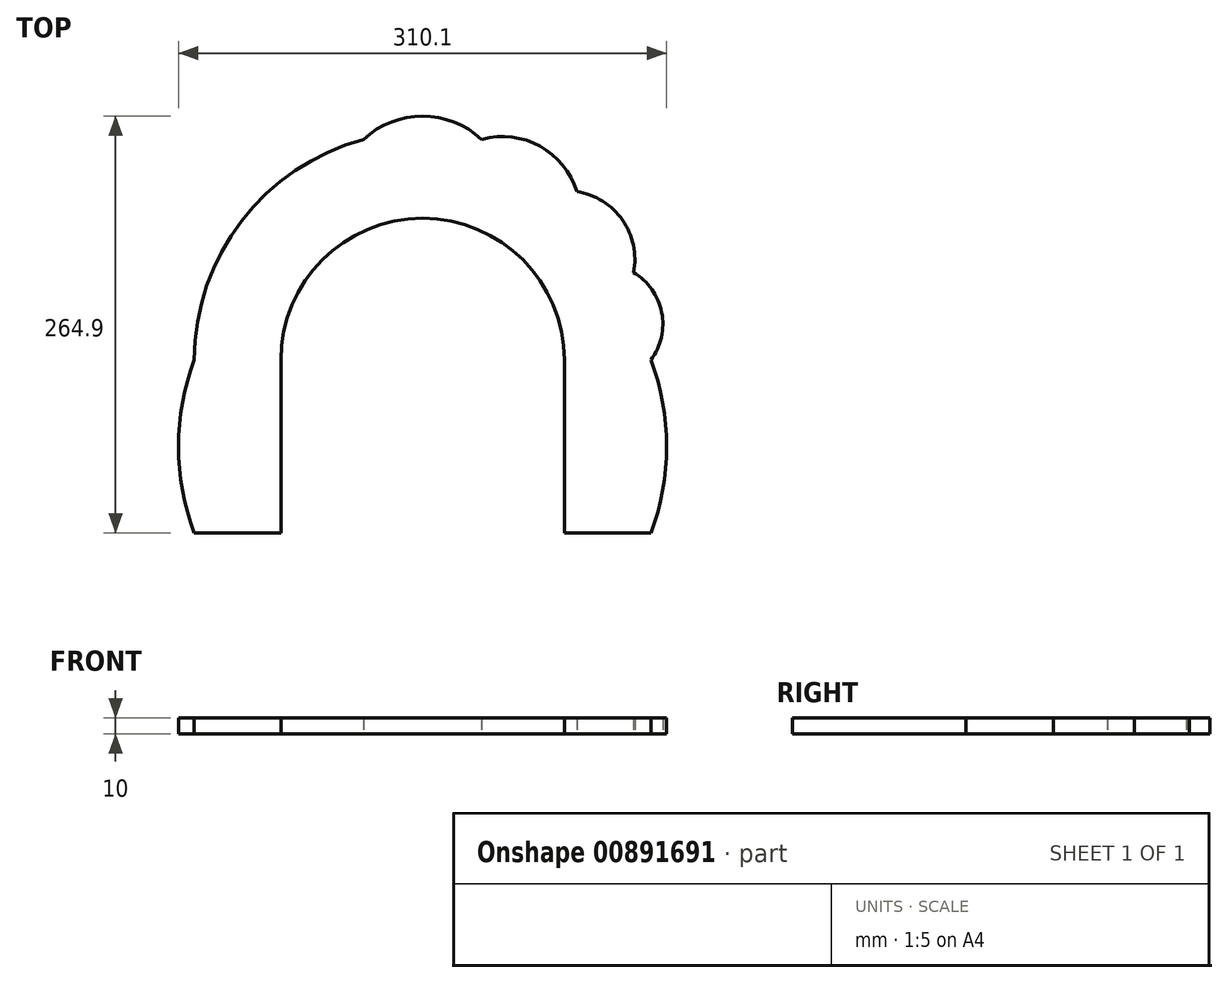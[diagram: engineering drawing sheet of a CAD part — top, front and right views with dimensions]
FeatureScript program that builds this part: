
annotation { "Feature Type Name" : "Feature", "Feature Type Description" : "" }
export const myFeature = defineFeature(function(context is Context, id is Id, definition is map)
    precondition{}
    {
        {
            var Q0;
            Q0=qCreatedBy(makeId("Top.planeOp"),FACE);
            var sketch = newSketch(context, id + "F0", { "sketchPlane" : qUnion([Q0])});
            skFitSpline(sketch, "E0.0.0", {"points": [v(222.24, 427.22) * mm, v(215.5, 429.07) * mm, v(196.44, 434.28) * mm, v(159.63, 464.69) * mm, v(135.76, 484.28) * mm]});
            skArc(sketch, "E0.0.1", {"start": v(135.76, 484.28) * mm, "mid": v(0, 567.46) * mm, "end": v(-135.76, 484.28) * mm});
            skFitSpline(sketch, "E0.0.2", {"points": [v(-135.76, 484.28) * mm, v(-159.63, 464.69) * mm, v(-196.44, 434.28) * mm, v(-215.5, 429.07) * mm, v(-222.24, 427.22) * mm]});
            skFitSpline(sketch, "E0.0.3", {"points": [v(-222.24, 427.22) * mm, v(-225.16, 426.83) * mm, v(-230.26, 426.14) * mm, v(-241.5, 428) * mm, v(-248.93, 433.28) * mm, v(-251.17, 448.34) * mm, v(-240.81, 458.85) * mm, v(-228.97, 457.5) * mm, v(-213.8, 449.01) * mm, v(-232.53, 431.49) * mm, v(-211.41, 442.33) * mm, v(-207.14, 460.38) * mm, v(-224.77, 474.32) * mm, v(-243.2, 474.95) * mm, v(-261.09, 471.32) * mm, v(-274.5, 457.58) * mm, v(-276.7, 439.28) * mm, v(-273.51, 422.75) * mm, v(-283.7, 412.03) * mm, v(-291.16, 413.34) * mm, v(-288.14, 420.98) * mm, v(-292.96, 429.6) * mm, v(-309.4, 438.45) * mm, v(-332.6, 439.06) * mm, v(-351.6, 426.46) * mm, v(-359.68, 415.35) * mm, v(-362.45, 400.5) * mm, v(-361.53, 389.94) * mm, v(-359.47, 382.27) * mm, v(-356.53, 382.37) * mm, v(-352.55, 399.36) * mm, v(-340.04, 407) * mm, v(-328.58, 408.28) * mm, v(-311.3, 404.6) * mm, v(-307.8, 389.6) * mm, v(-312.22, 380.89) * mm, v(-314.05, 379.09) * mm]});
            skArc(sketch, "E0.0.4", {"start": v(-309.42, 390.28) * mm, "mid": v(-312.68, 382.2) * mm, "end": v(-319.87, 377.3) * mm});
            skFitSpline(sketch, "E0.0.5", {"points": [v(-314.05, 379.09) * mm, v(-349.26, 368.46) * mm, v(-392.1, 351.55) * mm, v(-410.06, 337.43) * mm]});
            skEllipticalArc(sketch, "E0.0.6", {});
            skArc(sketch, "E0.0.7", {"start": v(-404.46, 196.44) * mm, "mid": v(-395.87, 191.21) * mm, "end": v(-386.4, 187.8) * mm});
            skFitSpline(sketch, "E0.0.8", {"points": [v(-394.78, 189.9) * mm, v(-344.92, 177.5) * mm, v(-241.75, 151.88) * mm, v(-181.26, 51.75) * mm, v(-150, 0) * mm]});
            skLineSegment(sketch, "E0.0.9", {"start": v(-150, 0) * mm, "end": v(-90, 0) * mm});
            skLineSegment(sketch, "E0.0.10", {"start": v(-90, 0) * mm, "end": v(-90, 110) * mm});
            skArc(sketch, "E0.0.11", {"start": v(-90, 110) * mm, "mid": v(0, 200) * mm, "end": v(90, 110) * mm});
            skLineSegment(sketch, "E0.0.12", {"start": v(90, 110) * mm, "end": v(90, 0) * mm});
            skLineSegment(sketch, "E0.0.13", {"start": v(90, 0) * mm, "end": v(150, 0) * mm});
            skFitSpline(sketch, "E0.0.14", {"points": [v(150, 0) * mm, v(181.26, 51.75) * mm, v(241.75, 151.88) * mm, v(344.92, 177.5) * mm, v(394.78, 189.9) * mm]});
            skArc(sketch, "E0.0.15", {"start": v(386.4, 187.8) * mm, "mid": v(395.87, 191.21) * mm, "end": v(404.46, 196.44) * mm});
            skEllipticalArc(sketch, "E0.0.16", {});
            skFitSpline(sketch, "E0.0.17", {"points": [v(410.06, 337.43) * mm, v(392.1, 351.55) * mm, v(349.26, 368.46) * mm, v(314.05, 379.09) * mm]});
            skArc(sketch, "E0.0.18", {"start": v(319.87, 377.3) * mm, "mid": v(312.68, 382.2) * mm, "end": v(309.42, 390.28) * mm});
            skFitSpline(sketch, "E0.0.19", {"points": [v(314.05, 379.09) * mm, v(312.22, 380.89) * mm, v(307.8, 389.6) * mm, v(311.3, 404.6) * mm, v(328.58, 408.28) * mm, v(340.04, 407) * mm, v(352.55, 399.36) * mm, v(356.53, 382.37) * mm, v(359.47, 382.27) * mm, v(361.53, 389.94) * mm, v(362.45, 400.5) * mm, v(359.68, 415.35) * mm, v(351.6, 426.46) * mm, v(332.6, 439.06) * mm, v(309.4, 438.45) * mm, v(292.96, 429.6) * mm, v(288.14, 420.98) * mm, v(291.16, 413.34) * mm, v(283.7, 412.03) * mm, v(273.51, 422.75) * mm, v(276.7, 439.28) * mm, v(274.5, 457.58) * mm, v(261.09, 471.32) * mm, v(243.2, 474.95) * mm, v(224.77, 474.32) * mm, v(207.14, 460.38) * mm, v(211.41, 442.33) * mm, v(232.53, 431.49) * mm, v(213.8, 449.01) * mm, v(228.97, 457.5) * mm, v(240.81, 458.85) * mm, v(251.17, 448.34) * mm, v(248.93, 433.28) * mm, v(241.5, 428) * mm, v(230.26, 426.14) * mm, v(225.16, 426.83) * mm, v(222.24, 427.22) * mm]});
            skLineSegment(sketch, "E1.0", {"start": v(-226.6, 290) * mm, "end": v(-165, 290) * mm});
            skLineSegment(sketch, "E1.1", {"start": v(-165, 290) * mm, "end": v(-165, 325.2) * mm});
            skLineSegment(sketch, "E1.2", {"start": v(-165, 325.2) * mm, "end": v(-226.6, 325.2) * mm});
            skLineSegment(sketch, "E1.3", {"start": v(-226.6, 290) * mm, "end": v(-226.6, 325.2) * mm});
            skLineSegment(sketch, "E1.4", {"start": v(-236.6, 290) * mm, "end": v(-236.6, 325.2) * mm});
            skLineSegment(sketch, "E1.5", {"start": v(-236.6, 325.2) * mm, "end": v(-298.2, 325.2) * mm});
            skLineSegment(sketch, "E1.6", {"start": v(-298.2, 290) * mm, "end": v(-236.6, 290) * mm});
            skLineSegment(sketch, "E1.7", {"start": v(-298.2, 290) * mm, "end": v(-298.2, 325.2) * mm});
            skLineSegment(sketch, "E2.0", {"start": v(-369.8, 290) * mm, "end": v(-308.2, 290) * mm});
            skLineSegment(sketch, "E3.0", {"start": v(-308.2, 325.2) * mm, "end": v(-369.8, 325.2) * mm});
            skLineSegment(sketch, "E4.0", {"start": v(-308.2, 290) * mm, "end": v(-308.2, 325.2) * mm});
            skLineSegment(sketch, "E5.0", {"start": v(-369.8, 290) * mm, "end": v(-369.8, 325.2) * mm});
            skFitSpline(sketch, "E6.0", {"points": [v(-342.67, 339.28) * mm, v(-317.97, 353.62) * mm, v(-277.69, 364.45) * mm, v(-252.88, 405.7) * mm, v(-252.65, 405.6) * mm, v(-252.66, 408.6) * mm]});
            skArc(sketch, "E7.0", {"start": v(-250.27, 406.87) * mm, "mid": v(-251.77, 407.17) * mm, "end": v(-252.75, 406) * mm});
            skFitSpline(sketch, "E8.0", {"points": [v(-250.27, 406.87) * mm, v(-244.43, 403.08) * mm, v(-228.6, 392.87) * mm, v(-192.33, 407.72) * mm, v(-169.18, 417.08) * mm]});
            skArc(sketch, "E9.0", {"start": v(-169.05, 414.28) * mm, "mid": v(-169.97, 415.86) * mm, "end": v(-171.8, 416.02) * mm});
            skFitSpline(sketch, "E10.0", {"points": [v(-168.95, 431.44) * mm, v(-171.46, 401.1) * mm, v(-158.84, 363.56) * mm, v(-169.18, 340.2) * mm]});
            skLineSegment(sketch, "E11.0", {"start": v(-226.24, 340.2) * mm, "end": v(-169.18, 340.2) * mm});
            skArc(sketch, "E12.0", {"start": v(-251.86, 357.45) * mm, "mid": v(-240.78, 346.25) * mm, "end": v(-226.24, 340.2) * mm});
            skArc(sketch, "E13.0", {"start": v(-252.03, 357.45) * mm, "mid": v(-263.1, 346.24) * mm, "end": v(-277.63, 340.17) * mm});
            skLineSegment(sketch, "E14.0", {"start": v(-331.71, 340.22) * mm, "end": v(-277.63, 340.17) * mm});
            skArc(sketch, "E15.0", {"start": v(-332.8, 344.66) * mm, "mid": v(-334, 342.02) * mm, "end": v(-331.71, 340.22) * mm});
            skArc(sketch, "E16.0", {"start": v(-251.86, 357.45) * mm, "mid": v(-251.95, 357.5) * mm, "end": v(-252.03, 357.45) * mm});
            skLineSegment(sketch, "E17.0", {"start": v(165, 290) * mm, "end": v(165, 325.2) * mm});
            skLineSegment(sketch, "E18.0", {"start": v(165, 290) * mm, "end": v(226.6, 290) * mm});
            skLineSegment(sketch, "E19.0", {"start": v(226.6, 290) * mm, "end": v(226.6, 325.2) * mm});
            skLineSegment(sketch, "E20.0", {"start": v(165, 325.2) * mm, "end": v(226.6, 325.2) * mm});
            skLineSegment(sketch, "E21.0", {"start": v(236.6, 325.2) * mm, "end": v(298.2, 325.2) * mm});
            skLineSegment(sketch, "E22.0", {"start": v(236.6, 290) * mm, "end": v(236.6, 325.2) * mm});
            skLineSegment(sketch, "E23.0", {"start": v(236.6, 290) * mm, "end": v(298.2, 290) * mm});
            skLineSegment(sketch, "E24.0", {"start": v(298.2, 290) * mm, "end": v(298.2, 325.2) * mm});
            skLineSegment(sketch, "E25.0", {"start": v(308.2, 290) * mm, "end": v(308.2, 325.2) * mm});
            skLineSegment(sketch, "E26.0", {"start": v(308.2, 325.2) * mm, "end": v(369.8, 325.2) * mm});
            skLineSegment(sketch, "E27.0", {"start": v(369.8, 290) * mm, "end": v(369.8, 325.2) * mm});
            skLineSegment(sketch, "E28.0", {"start": v(308.2, 290) * mm, "end": v(369.8, 290) * mm});
            skFitSpline(sketch, "E29.0", {"points": [v(342.67, 339.28) * mm, v(317.97, 353.62) * mm, v(277.69, 364.45) * mm, v(252.88, 405.7) * mm, v(252.65, 405.6) * mm, v(252.66, 408.6) * mm]});
            skArc(sketch, "E30.0", {"start": v(332.8, 344.66) * mm, "mid": v(334, 342.02) * mm, "end": v(331.71, 340.22) * mm});
            skLineSegment(sketch, "E31.0", {"start": v(331.71, 340.22) * mm, "end": v(277.63, 340.17) * mm});
            skArc(sketch, "E32.0", {"start": v(252.03, 357.45) * mm, "mid": v(263.1, 346.24) * mm, "end": v(277.63, 340.17) * mm});
            skArc(sketch, "E33.0", {"start": v(251.86, 357.45) * mm, "mid": v(240.78, 346.25) * mm, "end": v(226.24, 340.2) * mm});
            skArc(sketch, "E34.0", {"start": v(251.86, 357.45) * mm, "mid": v(251.95, 357.5) * mm, "end": v(252.03, 357.45) * mm});
            skLineSegment(sketch, "E35.0", {"start": v(226.24, 340.2) * mm, "end": v(169.18, 340.2) * mm});
            skFitSpline(sketch, "E36.0", {"points": [v(168.95, 431.44) * mm, v(171.46, 401.1) * mm, v(158.84, 363.56) * mm, v(169.18, 340.2) * mm]});
            skArc(sketch, "E37.0", {"start": v(169.05, 414.28) * mm, "mid": v(169.97, 415.86) * mm, "end": v(171.8, 416.02) * mm});
            skFitSpline(sketch, "E38.0", {"points": [v(250.27, 406.87) * mm, v(244.43, 403.08) * mm, v(228.6, 392.87) * mm, v(192.33, 407.72) * mm, v(169.18, 417.08) * mm]});
            skArc(sketch, "E39.0", {"start": v(250.27, 406.87) * mm, "mid": v(251.77, 407.17) * mm, "end": v(252.75, 406) * mm});
            skArc(sketch, "E40.0.0", {"start": v(367.9, 246.89) * mm, "mid": v(366.57, 245.65) * mm, "end": v(366.79, 243.85) * mm});
            skArc(sketch, "E40.0.1", {"start": v(366.79, 243.85) * mm, "mid": v(401.04, 245.6) * mm, "end": v(383.39, 275) * mm});
            skLineSegment(sketch, "E40.0.2", {"start": v(383.39, 275) * mm, "end": v(-383.39, 275) * mm});
            skArc(sketch, "E40.0.3", {"start": v(-383.39, 275) * mm, "mid": v(-401.04, 245.6) * mm, "end": v(-366.79, 243.85) * mm});
            skArc(sketch, "E40.0.4", {"start": v(-366.79, 243.85) * mm, "mid": v(-366.57, 245.65) * mm, "end": v(-367.9, 246.89) * mm});
            skEllipticalArc(sketch, "E40.0.5", {});
            skArc(sketch, "E40.0.6", {"start": v(-369.23, 261.25) * mm, "mid": v(-358.46, 257.25) * mm, "end": v(-353.55, 246.86) * mm});
            skArc(sketch, "E40.0.7", {"start": v(-353.55, 246.86) * mm, "mid": v(-353.08, 242.95) * mm, "end": v(-352.1, 239.13) * mm});
            skFitSpline(sketch, "E40.0.8", {"points": [v(-353.7, 243.85) * mm, v(-350.61, 235.19) * mm, v(-342.3, 200.93) * mm, v(-287.54, 161.27) * mm, v(-255.18, 135.34) * mm]});
            skFitSpline(sketch, "E40.0.9", {"points": [v(-394.78, 189.9) * mm, v(-344.92, 177.5) * mm, v(-241.75, 151.88) * mm, v(-181.26, 51.75) * mm, v(-150, 0) * mm]});
            skFitSpline(sketch, "E40.0.15", {"points": [v(150, 0) * mm, v(181.26, 51.75) * mm, v(241.75, 151.88) * mm, v(344.92, 177.5) * mm, v(394.78, 189.9) * mm]});
            skFitSpline(sketch, "E40.0.16", {"points": [v(255.18, 135.34) * mm, v(287.54, 161.27) * mm, v(342.3, 200.93) * mm, v(350.61, 235.19) * mm, v(353.7, 243.85) * mm]});
            skArc(sketch, "E40.0.17", {"start": v(352.1, 239.13) * mm, "mid": v(353.08, 242.95) * mm, "end": v(353.55, 246.86) * mm});
            skArc(sketch, "E40.0.18", {"start": v(353.55, 246.86) * mm, "mid": v(358.46, 257.25) * mm, "end": v(369.23, 261.25) * mm});
            skEllipticalArc(sketch, "E40.0.19", {});
            skLineSegment(sketch, "E41.0.0", {"start": v(305.94, 275) * mm, "end": v(-305.94, 275) * mm});
            skArc(sketch, "E41.0.1", {"start": v(-305.94, 275) * mm, "mid": v(-327.36, 237.1) * mm, "end": v(-283.84, 238.31) * mm});
            skArc(sketch, "E41.0.2", {"start": v(-283.84, 238.31) * mm, "mid": v(-283.78, 240.06) * mm, "end": v(-285.12, 241.19) * mm});
            skEllipticalArc(sketch, "E41.0.3", {});
            skFitSpline(sketch, "E41.0.4", {"points": [v(-286.27, 259.2) * mm, v(1000, -265.74) * mm, v(256.47, 1000) * mm]});
            skFitSpline(sketch, "E41.0.5", {"points": [v(-285.63, 259.1) * mm, v(1000, -265.14) * mm, v(258.09, 1000) * mm]});
            skFitSpline(sketch, "E41.0.6", {"points": [v(-265.5, 243.26) * mm, v(-263.97, 221.32) * mm, v(-260.75, 173.86) * mm, v(-230.38, 123.02) * mm, v(-214.22, 95.6) * mm]});
            skFitSpline(sketch, "E41.0.7", {"points": [v(-394.78, 189.9) * mm, v(-344.92, 177.5) * mm, v(-241.75, 151.88) * mm, v(-181.26, 51.75) * mm, v(-150, 0) * mm]});
            skFitSpline(sketch, "E41.0.13", {"points": [v(150, 0) * mm, v(181.26, 51.75) * mm, v(241.75, 151.88) * mm, v(344.92, 177.5) * mm, v(394.78, 189.9) * mm]});
            skFitSpline(sketch, "E41.0.14", {"points": [v(214.22, 95.6) * mm, v(230.38, 123.02) * mm, v(260.75, 173.86) * mm, v(263.97, 221.32) * mm, v(265.5, 243.26) * mm]});
            skFitSpline(sketch, "E41.0.15", {"points": [v(265.14, 238.31) * mm, v(1000, 265.14) * mm, v(258.09, 1000) * mm]});
            skLineSegment(sketch, "E41.0.16", {"start": v(285.63, 259.1) * mm, "end": v(286.27, 259.2) * mm});
            skEllipticalArc(sketch, "E41.0.17", {});
            skArc(sketch, "E41.0.18", {"start": v(285.12, 241.19) * mm, "mid": v(283.78, 240.06) * mm, "end": v(283.84, 238.31) * mm});
            skArc(sketch, "E41.0.19", {"start": v(283.84, 238.31) * mm, "mid": v(327.36, 237.1) * mm, "end": v(305.94, 275) * mm});
            skArc(sketch, "E42.0.0", {"start": v(188.69, 224.82) * mm, "mid": v(238.32, 232.86) * mm, "end": v(210.88, 275) * mm});
            skLineSegment(sketch, "E42.0.1", {"start": v(210.88, 275) * mm, "end": v(-210.88, 275) * mm});
            skArc(sketch, "E42.0.2", {"start": v(-210.88, 275) * mm, "mid": v(-238.32, 232.86) * mm, "end": v(-188.69, 224.82) * mm});
            skArc(sketch, "E42.0.3", {"start": v(-188.69, 224.82) * mm, "mid": v(-188.58, 226.71) * mm, "end": v(-190.1, 227.85) * mm});
            skEllipticalArc(sketch, "E42.0.4", {});
            skFitSpline(sketch, "E42.0.5", {"points": [v(-190.78, 251.9) * mm, v(1000, -168.95) * mm, v(251.9, 1000) * mm]});
            skArc(sketch, "E42.0.6", {"start": v(-170.52, 233.6) * mm, "mid": v(-170.48, 227.5) * mm, "end": v(-171.67, 221.5) * mm});
            skFitSpline(sketch, "E42.0.7", {"points": [v(-170.36, 225.76) * mm, v(-179.25, 197.05) * mm, v(-199.12, 132.86) * mm, v(-167.48, 47.3) * mm, v(-150, 0) * mm]});
            skFitSpline(sketch, "E42.0.13", {"points": [v(150, 0) * mm, v(167.48, 47.3) * mm, v(199.12, 132.86) * mm, v(179.25, 197.05) * mm, v(170.36, 225.76) * mm]});
            skArc(sketch, "E42.0.14", {"start": v(171.67, 221.5) * mm, "mid": v(170.48, 227.5) * mm, "end": v(170.52, 233.6) * mm});
            skFitSpline(sketch, "E42.0.15", {"points": [v(170.36, 225.76) * mm, v(1000, 168.95) * mm, v(251.9, 1000) * mm]});
            skEllipticalArc(sketch, "E42.0.16", {});
            skArc(sketch, "E42.0.17", {"start": v(190.1, 227.85) * mm, "mid": v(188.58, 226.71) * mm, "end": v(188.69, 224.82) * mm});
            const initialGuessF0  = {"E0.0.6": [-0.34931216680627963, 0.26310522471521947, -0.8795186508433591, 0.4758644164241295, 0.09801349999999999, 0.086147, 5.8461119226871325, 1.3987543209554119], "E0.0.16": [0.34931216680627963, 0.26310522471521947, 0.8795186508433591, 0.4758644164241295, 0.09801349999999999, 0.086147, 4.884430986224174, 0.4370733844924535], "E40.0.5": [-0.3692299729374505, 0.25402610760164496, -1, 0, 0.00868, 0.0072229875998473525, 4.71238898038469, 1.7242785659408997], "E40.0.19": [0.3692299729374472, 0.2540261076016343, 1, 0, 0.00868, 0.0072229875998473525, 4.558906741237017, 1.5707963267948966], "E41.0.3": [-0.2862692176634982, 0.25016623719894915, 1, 0, 0.01114790895395411, 0.00902888915716235, 1.5707963267948966, 4.816091749526819], "E41.0.17": [0.28626921761494883, 0.25016623719894915, 1, 0, 0.01114790895395411, 0.00902888915716235, 4.6086862112438105, 1.5707963267948968], "E42.0.4": [-0.19077662931411604, 0.2398668370838165, -1, 0, 0.012873693325351057, 0.012037203490749382, 4.71238898038469, 1.6233236227230905], "E42.0.16": [0.19077662931381673, 0.2398668370838165, -1, 0, 0.012873693325351057, 0.012037203490749382, 1.5182690308667026, 4.71238898038469]};
            skSetInitialGuess(sketch, initialGuessF0);
            skSolve(sketch);
        }
        {
            var Q0;
            Q0=qCreatedBy(makeId("Top.planeOp"),FACE);
            var sketch = newSketch(context, id + "F1", { "sketchPlane" : qUnion([Q0])});
            skLineSegment(sketch, "E43.0", {"start": v(105, 110) * mm, "end": v(105, 0) * mm});
            skArc(sketch, "E43.1", {"start": v(-105, 110) * mm, "mid": v(0, 215) * mm, "end": v(105, 110) * mm});
            skLineSegment(sketch, "E43.2", {"start": v(-105, 0) * mm, "end": v(-105, 110) * mm});
            skLineSegment(sketch, "E44.0", {"start": v(145, 110) * mm, "end": v(145, 0) * mm});
            skArc(sketch, "E44.1", {"start": v(-145, 110) * mm, "mid": v(0, 255) * mm, "end": v(145, 110) * mm});
            skLineSegment(sketch, "E44.2", {"start": v(-145, 0) * mm, "end": v(-145, 110) * mm});
            skLineSegment(sketch, "E45.0", {"start": v(125, 110) * mm, "end": v(125, 0) * mm, "construction": true});
            skArc(sketch, "E45.1", {"start": v(-125, 110) * mm, "mid": v(0, 235) * mm, "end": v(125, 110) * mm, "construction": true});
            skLineSegment(sketch, "E45.2", {"start": v(-125, 0) * mm, "end": v(-125, 110) * mm, "construction": true});
            skLineSegment(sketch, "E46.direction1", {"start": v(125, 20) * mm, "end": v(150, 20) * mm, "construction": true});
            skLineSegment(sketch, "E47.direction2", {"start": v(125, 20) * mm, "end": v(125, 65) * mm, "construction": true});
            skLineSegment(sketch, "E48.0", {"start": v(155, 110) * mm, "end": v(155, 0) * mm, "construction": true});
            skArc(sketch, "E48.1", {"start": v(-155, 110) * mm, "mid": v(0, 265) * mm, "end": v(155, 110) * mm, "construction": true});
            skLineSegment(sketch, "E48.2", {"start": v(-155, 0) * mm, "end": v(-155, 110) * mm, "construction": true});
            skArc(sketch, "E49", {"start": v(145, 0) * mm, "mid": v(155.05, 55) * mm, "end": v(145, 110) * mm});
            skArc(sketch, "E50", {"start": v(145, 110) * mm, "mid": v(151.89, 140.21) * mm, "end": v(133.96, 165.49) * mm});
            skArc(sketch, "E51", {"start": v(133.96, 165.49) * mm, "mid": v(126.95, 198.9) * mm, "end": v(97.96, 216.9) * mm});
            skArc(sketch, "E52", {"start": v(97.96, 216.9) * mm, "mid": v(74.5, 245.79) * mm, "end": v(37.53, 250.06) * mm});
            skArc(sketch, "E53", {"start": v(37.53, 250.06) * mm, "mid": v(0, 264.9) * mm, "end": v(-37.53, 250.06) * mm});
            skArc(sketch, "E54.MirrorCS", {"start": v(-97.96, 216.9) * mm, "mid": v(-74.5, 245.79) * mm, "end": v(-37.53, 250.06) * mm});
            skArc(sketch, "E55.MirrorCS", {"start": v(-133.96, 165.49) * mm, "mid": v(-126.95, 198.9) * mm, "end": v(-97.96, 216.9) * mm});
            skArc(sketch, "E56.MirrorCS", {"start": v(-145, 110) * mm, "mid": v(-151.89, 140.21) * mm, "end": v(-133.96, 165.49) * mm});
            skArc(sketch, "E57.MirrorCS", {"start": v(-145, 0) * mm, "mid": v(-155.05, 55) * mm, "end": v(-145, 110) * mm});
            skLineSegment(sketch, "E58", {"start": v(-145, 0) * mm, "end": v(-105, 0) * mm});
            skLineSegment(sketch, "E59", {"start": v(105, 0) * mm, "end": v(145, 0) * mm});
            skLineSegment(sketch, "E60.0", {"start": v(-90, 0) * mm, "end": v(-90, 110) * mm});
            skArc(sketch, "E61.0", {"start": v(-90, 110) * mm, "mid": v(0, 200) * mm, "end": v(90, 110) * mm});
            skLineSegment(sketch, "E62.0", {"start": v(90, 110) * mm, "end": v(90, 0) * mm});
            skLineSegment(sketch, "E63.0", {"start": v(90, 0) * mm, "end": v(150, 0) * mm});
            skLineSegment(sketch, "E64", {"start": v(-105, 0) * mm, "end": v(-90, 0) * mm});
            skSolve(sketch);
        }
        {
            var Q0;
            {var subQ7=sQuery(id+"F1.wireOp",EDGE,"E43.0");Q0=makeQuery(id+"F1.imprint","IMPRINT",FACE,{"disambiguationData":[TD([[makeQuery(id+"F1.imprint","IMPRINT",EDGE,{"derivedFrom":subQ7}),1.0]])]});}
            var Q1;
            Q1=makeQuery(id+"F1.imprint","IMPRINT",FACE,{"disambiguationData":[TD([[makeQuery(id+"F1.imprint","IMPRINT",EDGE,{"derivedFrom":sQuery(id+"F1.wireOp",EDGE,"E44.2")}),1.0]])]});
            var Q2;
            {var subQ0=sQuery(id+"F1.wireOp",EDGE,"E56.MirrorCS");Q2=makeQuery(id+"F1.imprint","IMPRINT",FACE,{"disambiguationData":[TD([[makeQuery(id+"F1.imprint","IMPRINT",EDGE,{"derivedFrom":subQ0}),-1.0]])]});}
            var Q3;
            {var subQ0=sQuery(id+"F1.wireOp",EDGE,"E55.MirrorCS");Q3=makeQuery(id+"F1.imprint","IMPRINT",FACE,{"disambiguationData":[TD([[makeQuery(id+"F1.imprint","IMPRINT",EDGE,{"derivedFrom":subQ0}),-1.0]])]});}
            var Q4;
            {var subQ0=sQuery(id+"F1.wireOp",EDGE,"E54.MirrorCS");Q4=makeQuery(id+"F1.imprint","IMPRINT",FACE,{"disambiguationData":[TD([[makeQuery(id+"F1.imprint","IMPRINT",EDGE,{"derivedFrom":subQ0}),-1.0]])]});}
            var Q5;
            {var subQ0=sQuery(id+"F1.wireOp",EDGE,"E53");Q5=makeQuery(id+"F1.imprint","IMPRINT",FACE,{"disambiguationData":[TD([[makeQuery(id+"F1.imprint","IMPRINT",EDGE,{"derivedFrom":subQ0}),1.0]])]});}
            var Q6;
            {var subQ0=sQuery(id+"F1.wireOp",EDGE,"E52");Q6=makeQuery(id+"F1.imprint","IMPRINT",FACE,{"disambiguationData":[TD([[makeQuery(id+"F1.imprint","IMPRINT",EDGE,{"derivedFrom":subQ0}),1.0]])]});}
            var Q7;
            {var subQ0=sQuery(id+"F1.wireOp",EDGE,"E51");Q7=makeQuery(id+"F1.imprint","IMPRINT",FACE,{"disambiguationData":[TD([[makeQuery(id+"F1.imprint","IMPRINT",EDGE,{"derivedFrom":subQ0}),1.0]])]});}
            var Q8;
            {var subQ0=sQuery(id+"F1.wireOp",EDGE,"E50");Q8=makeQuery(id+"F1.imprint","IMPRINT",FACE,{"disambiguationData":[TD([[makeQuery(id+"F1.imprint","IMPRINT",EDGE,{"derivedFrom":subQ0}),1.0]])]});}
            var Q9;
            Q9=makeQuery(id+"F1.imprint","IMPRINT",FACE,{"disambiguationData":[TD([[makeQuery(id+"F1.imprint","IMPRINT",EDGE,{"derivedFrom":sQuery(id+"F1.wireOp",EDGE,"E44.0")}),1.0]])]});
            var Q10;
            {var subQ0=sQuery(id+"F1.wireOp",EDGE,"E43.0");Q10=makeQuery(id+"F1.imprint","IMPRINT",FACE,{"disambiguationData":[TD([[makeQuery(id+"F1.imprint","IMPRINT",EDGE,{"derivedFrom":subQ0}),-1.0]])]});}
            extrude(context, id + "F2", {"entities" : qUnion([Q0, Q1, Q2, Q3, Q4, Q5, Q6, Q7, Q8, Q9, Q10]), "depth" : 10 * mm, "offsetDistance" : 25 * mm});
        }
        {
            var Q0;
            Q0=makeQuery(id+"F2.opExtrude","CAP_FACE",FACE,{"disambiguationData":[OSD([sQuery(id+"F1.wireOp",EDGE,"E49"),sQuery(id+"F1.wireOp",EDGE,"E50"),sQuery(id+"F1.wireOp",EDGE,"E51"),sQuery(id+"F1.wireOp",EDGE,"E52"),sQuery(id+"F1.wireOp",EDGE,"E53"),sQuery(id+"F1.wireOp",EDGE,"E54.MirrorCS"),sQuery(id+"F1.wireOp",EDGE,"E55.MirrorCS"),sQuery(id+"F1.wireOp",EDGE,"E56.MirrorCS"),sQuery(id+"F1.wireOp",EDGE,"E57.MirrorCS"),sQuery(id+"F1.wireOp",EDGE,"E58"),sQuery(id+"F1.wireOp",EDGE,"E60.0"),sQuery(id+"F1.wireOp",EDGE,"E61.0"),sQuery(id+"F1.wireOp",EDGE,"E62.0"),sQuery(id+"F1.wireOp",EDGE,"E63.0"),sQuery(id+"F1.wireOp",EDGE,"E64")])],"isStart":false});
            cPlane(context, id + "F3", {"entities" : qUnion([Q0]), "cplaneType" : CPlaneType.OFFSET, "offset" : 50 * mm, "width" : 150 * mm, "height" : 150 * mm});
        }
    });
